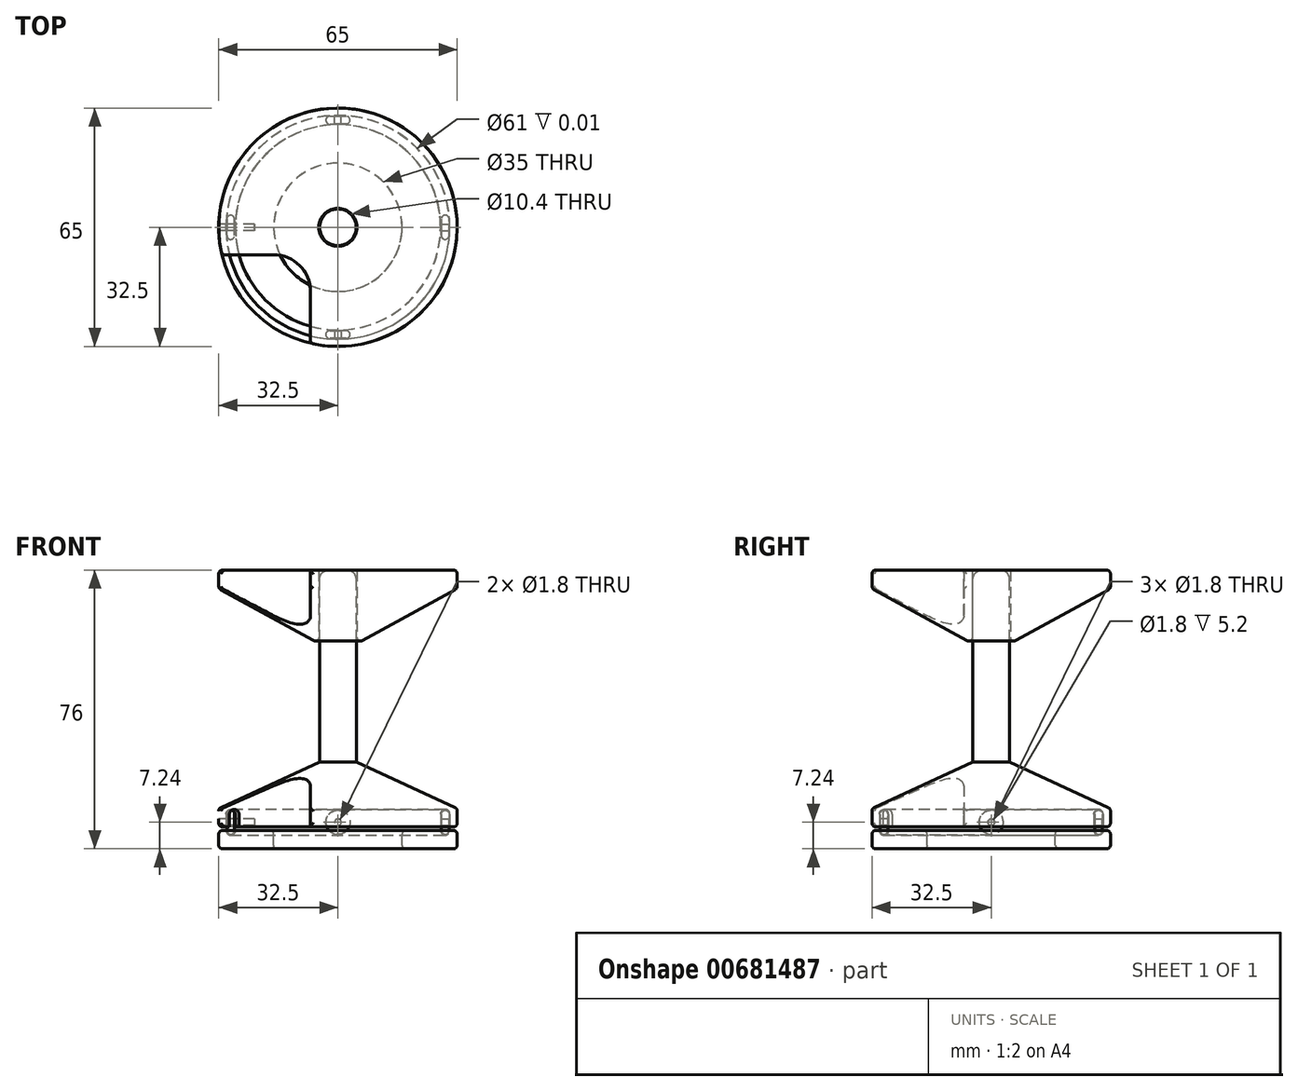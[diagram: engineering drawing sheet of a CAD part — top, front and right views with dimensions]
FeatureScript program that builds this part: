
annotation { "Feature Type Name" : "Feature", "Feature Type Description" : "" }
export const myFeature = defineFeature(function(context is Context, id is Id, definition is map)
    precondition{}
    {
        {
            var Q0;
            Q0=qCreatedBy(makeId("Front.planeOp"),FACE);
            var sketch = newSketch(context, id + "F0", { "sketchPlane" : qUnion([Q0])});
            skLineSegment(sketch, "E0.bottom", {"start": v(0, 2.5) * mm, "end": v(-17.5, 2.5) * mm, "construction": true});
            skLineSegment(sketch, "E0.top", {"start": v(0, -2.5) * mm, "end": v(-17.5, -2.5) * mm, "construction": true});
            skLineSegment(sketch, "E0.left", {"start": v(0, 2.5) * mm, "end": v(0, -2.5) * mm, "construction": true});
            skLineSegment(sketch, "E0.right", {"start": v(-32.5, 2.5) * mm, "end": v(-32.5, -2.5) * mm});
            skPoint(sketch, "E1", {"position": v(-30.5, 2.5) * mm});
            skPoint(sketch, "E2", {"position": v(-28, 2.5) * mm});
            skLineSegment(sketch, "E3", {"start": v(-30.5, 2.5) * mm, "end": v(-30.5, 2.5) * mm});
            skLineSegment(sketch, "E4", {"start": v(-28, 2.5) * mm, "end": v(-28, 2.5) * mm});
            skLineSegment(sketch, "E5", {"start": v(-30.5, 2.5) * mm, "end": v(-28, 2.5) * mm, "construction": true});
            skArc(sketch, "E6", {"start": v(-30.5, 2.5) * mm, "mid": v(-29.25, 1.24) * mm, "end": v(-28, 2.5) * mm});
            skLineSegment(sketch, "E7.trimOffspring", {"start": v(-30.5, 2.5) * mm, "end": v(-32.5, 2.5) * mm});
            skLineSegment(sketch, "E8", {"start": v(-17.5, 2.5) * mm, "end": v(-17.5, -2.5) * mm});
            skLineSegment(sketch, "E9", {"start": v(-17.5, 2.5) * mm, "end": v(-28, 2.5) * mm});
            skLineSegment(sketch, "E10", {"start": v(-17.5, -2.5) * mm, "end": v(-32.5, -2.5) * mm});
            skSolve(sketch);
        }
        {
            var Q0;
            Q0 = qSketchRegion(id + "F0", true);
            var Q1;
            Q1=sQuery(id+"F0.wireOp",EDGE,"E0.left");
            revolve(context, id + "F1", {"entities" : qUnion([Q0]), "axis" : qUnion([Q1]), "revolveType" : RevolveType.FULL});
        }
        {
            var Q0;
            Q0=makeQuery(id+"F1.opRevolve","SWEPT_EDGE",EDGE,{"disambiguationData":[OSD([sQuery(id+"F0.wireOp",EDGE,"E0.right"),sQuery(id+"F0.wireOp",EDGE,"E7.trimOffspring")])]});
            var Q1;
            Q1=makeQuery(id+"F1.opRevolve","SWEPT_EDGE",EDGE,{"disambiguationData":[OSD([sQuery(id+"F0.wireOp",EDGE,"E8"),sQuery(id+"F0.wireOp",EDGE,"E9")])]});
            var Q2;
            Q2=makeQuery(id+"F1.opRevolve","SWEPT_EDGE",EDGE,{"disambiguationData":[OSD([sQuery(id+"F0.wireOp",EDGE,"E0.right"),sQuery(id+"F0.wireOp",EDGE,"E10")])]});
            var Q3;
            Q3=makeQuery(id+"F1.opRevolve","SWEPT_EDGE",EDGE,{"disambiguationData":[OSD([sQuery(id+"F0.wireOp",EDGE,"E8"),sQuery(id+"F0.wireOp",EDGE,"E10")])]});
            fillet(context, id + "F2", {"entities" : qUnion([Q0, Q1, Q2, Q3]), "radius" : 1 * mm, "tangentPropagation" : true, "allowEdgeOverflow" : false});
        }
        {
            var Q0;
            Q0=qCreatedBy(makeId("Front.planeOp"),FACE);
            var sketch = newSketch(context, id + "F3", { "sketchPlane" : qUnion([Q0])});
            skLineSegment(sketch, "E11.bottom", {"start": v(0, 8.5) * mm, "end": v(-32.5, 8.5) * mm, "construction": true});
            skLineSegment(sketch, "E11.top", {"start": v(0, 3.5) * mm, "end": v(-32.5, 3.5) * mm});
            skLineSegment(sketch, "E11.left", {"start": v(0, 23.5) * mm, "end": v(0, 3.5) * mm});
            skLineSegment(sketch, "E11.right", {"start": v(-32.5, 8.5) * mm, "end": v(-32.5, 3.5) * mm});
            skLineSegment(sketch, "E12", {"start": v(-32.5, 8.5) * mm, "end": v(-5, 21.2) * mm});
            skLineSegment(sketch, "E13", {"start": v(0, 23.5) * mm, "end": v(0, 73.5) * mm});
            skLineSegment(sketch, "E14", {"start": v(0, 73.5) * mm, "end": v(-5, 73.5) * mm});
            skLineSegment(sketch, "E15", {"start": v(-5, 73.5) * mm, "end": v(-5, 21.2) * mm});
            skLineSegment(sketch, "E16", {"start": v(-5, 21.2) * mm, "end": v(0, 23.5) * mm, "construction": true});
            skSolve(sketch);
        }
        {
            var Q0;
            Q0 = qSketchRegion(id + "F3", true);
            var Q1;
            Q1=sQuery(id+"F3.wireOp",EDGE,"E11.left");
            revolve(context, id + "F4", {"entities" : qUnion([Q0]), "axis" : qUnion([Q1]), "revolveType" : RevolveType.FULL});
        }
        {
            var Q0;
            Q0=makeQuery(id+"F4.opRevolve","SWEPT_EDGE",EDGE,{"disambiguationData":[OSD([sQuery(id+"F3.wireOp",EDGE,"E14"),sQuery(id+"F3.wireOp",EDGE,"E15")])]});
            fillet(context, id + "F5", {"entities" : qUnion([Q0]), "radius" : 2.5 * mm, "tangentPropagation" : true, "allowEdgeOverflow" : false});
        }
        {
            var Q0;
            Q0=makeQuery(id+"F4.opRevolve","SWEPT_FACE",FACE,{"disambiguationData":[OSD([sQuery(id+"F3.wireOp",EDGE,"E11.top")])]});
            cPlane(context, id + "F6", {"entities" : qUnion([Q0]), "cplaneType" : CPlaneType.OFFSET, "offset" : 0.5 * mm, "width" : 150 * mm, "height" : 150 * mm});
        }
        {
            var Q0;
            Q0=qCreatedBy(id+"F6.planeOp",FACE);
            var sketch = newSketch(context, id + "F7", { "sketchPlane" : qUnion([Q0])});
            skCircle(sketch, "E17", {"center": v(0, 0) * mm, "radius": 32.5 * mm, "construction": true});
            skLineSegment(sketch, "E18", {"start": v(-7.5, 49.07) * mm, "end": v(-7.5, 17.5) * mm});
            skLineSegment(sketch, "E19", {"start": v(-17.5, 7.5) * mm, "end": v(-49.07, 7.5) * mm});
            skLineSegment(sketch, "E20", {"start": v(-49.07, 7.5) * mm, "end": v(-7.5, 49.07) * mm});
            skPoint(sketch, "E21.visualSharp", {"position": v(-7.5, 7.5) * mm});
            skArc(sketch, "E21.filletArc", {"start": v(-17.5, 7.5) * mm, "mid": v(-10.43, 10.43) * mm, "end": v(-7.5, 17.5) * mm});
            skSolve(sketch);
        }
        {
            var Q0;
            Q0 = qSketchRegion(id + "F7", true);
            extrude(context, id + "F8", {"entities" : qUnion([Q0]), "operationType" : NewBodyOperationType.REMOVE, "oppositeDirection" : true, "depth" : 25 * mm, "offsetDistance" : 25 * mm});
        }
        {
            var Q0;
            Q0=makeQuery(id+"F4.opRevolve","SWEPT_EDGE",EDGE,{"disambiguationData":[OSD([sQuery(id+"F3.wireOp",EDGE,"E11.right"),sQuery(id+"F3.wireOp",EDGE,"E12")])]});
            var Q1;
            Q1=makeQuery(id+"F4.opRevolve","SWEPT_EDGE",EDGE,{"disambiguationData":[OSD([sQuery(id+"F3.wireOp",EDGE,"E11.top"),sQuery(id+"F3.wireOp",EDGE,"E11.right")])]});
            var Q2;
            {var subQ0=sQuery(id+"F7.wireOp",EDGE,"E19");Q2=makeQuery(id+"FT7dUQ1MtdXTtgQ_2.2.F8.boolean.opBoolean","INTERSECT",EDGE,{"derivedFrom":[makeQuery(id+"FT7dUQ1MtdXTtgQ_2.1.F8.boolean.opBoolean","SPLIT",FACE,{"disambiguationData":[TD([makeQuery(id+"F8.boolean.opBoolean","COPY",FACE,{"derivedFrom":makeQuery(id+"F8.opExtrude","SWEPT_FACE",FACE,{"disambiguationData":[OSD([subQ0])]})})])],"derivedFrom":makeQuery(id+"F4.opRevolve","SWEPT_FACE",FACE,{"disambiguationData":[OSD([sQuery(id+"F3.wireOp",EDGE,"E11.right")])]})}),makeQuery(id+"FT7dUQ1MtdXTtgQ_2.2.F8.opExtrude","SWEPT_FACE",FACE,{"disambiguationData":[OSD([subQ0])]})]});}
            var Q3;
            Q3=makeQuery(id+"FT7dUQ1MtdXTtgQ_2.1.F8.boolean.opBoolean","INTERSECT",EDGE,{"derivedFrom":[makeQuery(id+"F4.opRevolve","SWEPT_FACE",FACE,{"disambiguationData":[OSD([sQuery(id+"F3.wireOp",EDGE,"E11.right")])]}),makeQuery(id+"FT7dUQ1MtdXTtgQ_2.1.F8.opExtrude","SWEPT_FACE",FACE,{"disambiguationData":[OSD([sQuery(id+"F7.wireOp",EDGE,"E18")])]})]});
            var Q4;
            Q4=makeQuery(id+"FT7dUQ1MtdXTtgQ_2.1.F8.boolean.opBoolean","INTERSECT",EDGE,{"derivedFrom":[makeQuery(id+"F4.opRevolve","SWEPT_FACE",FACE,{"disambiguationData":[OSD([sQuery(id+"F3.wireOp",EDGE,"E12")])]}),makeQuery(id+"FT7dUQ1MtdXTtgQ_2.1.F8.opExtrude","SWEPT_FACE",FACE,{"disambiguationData":[OSD([sQuery(id+"F7.wireOp",EDGE,"E21.filletArc")])]})]});
            var Q5;
            Q5=makeQuery(id+"FT7dUQ1MtdXTtgQ_2.1.F8.boolean.opBoolean","INTERSECT",EDGE,{"derivedFrom":[makeQuery(id+"F4.opRevolve","SWEPT_FACE",FACE,{"disambiguationData":[OSD([sQuery(id+"F3.wireOp",EDGE,"E11.right")])]}),makeQuery(id+"FT7dUQ1MtdXTtgQ_2.1.F8.opExtrude","SWEPT_FACE",FACE,{"disambiguationData":[OSD([sQuery(id+"F7.wireOp",EDGE,"E19")])]})]});
            var Q6;
            Q6=makeQuery(id+"F8.boolean.opBoolean","INTERSECT",EDGE,{"derivedFrom":[makeQuery(id+"F4.opRevolve","SWEPT_FACE",FACE,{"disambiguationData":[OSD([sQuery(id+"F3.wireOp",EDGE,"E11.right")])]}),makeQuery(id+"F8.opExtrude","SWEPT_FACE",FACE,{"disambiguationData":[OSD([sQuery(id+"F7.wireOp",EDGE,"E18")])]})]});
            var Q7;
            Q7=makeQuery(id+"F8.boolean.opBoolean","INTERSECT",EDGE,{"derivedFrom":[makeQuery(id+"F4.opRevolve","SWEPT_FACE",FACE,{"disambiguationData":[OSD([sQuery(id+"F3.wireOp",EDGE,"E12")])]}),makeQuery(id+"F8.opExtrude","SWEPT_FACE",FACE,{"disambiguationData":[OSD([sQuery(id+"F7.wireOp",EDGE,"E21.filletArc")])]})]});
            var Q8;
            Q8=makeQuery(id+"F8.boolean.opBoolean","INTERSECT",EDGE,{"derivedFrom":[makeQuery(id+"F4.opRevolve","SWEPT_FACE",FACE,{"disambiguationData":[OSD([sQuery(id+"F3.wireOp",EDGE,"E11.right")])]}),makeQuery(id+"F8.opExtrude","SWEPT_FACE",FACE,{"disambiguationData":[OSD([sQuery(id+"F7.wireOp",EDGE,"E19")])]})]});
            var Q9;
            {var subQ0=sQuery(id+"F7.wireOp",EDGE,"E18");var subQ3=makeQuery(id+"F8.boolean.opBoolean","COPY",FACE,{"derivedFrom":makeQuery(id+"F8.opExtrude","SWEPT_FACE",FACE,{"disambiguationData":[OSD([sQuery(id+"F7.wireOp",EDGE,"E19")])]})});Q9=makeQuery(id+"FT7dUQ1MtdXTtgQ_2.3.F8.boolean.opBoolean","INTERSECT",EDGE,{"derivedFrom":[makeQuery(id+"FT7dUQ1MtdXTtgQ_2.2.F8.boolean.opBoolean","SPLIT",FACE,{"disambiguationData":[TD([subQ3])],"derivedFrom":makeQuery(id+"FT7dUQ1MtdXTtgQ_2.1.F8.boolean.opBoolean","SPLIT",FACE,{"disambiguationData":[TD([subQ3])],"derivedFrom":makeQuery(id+"F4.opRevolve","SWEPT_FACE",FACE,{"disambiguationData":[OSD([sQuery(id+"F3.wireOp",EDGE,"E11.right")])]})})}),makeQuery(id+"FT7dUQ1MtdXTtgQ_2.3.F8.opExtrude","SWEPT_FACE",FACE,{"disambiguationData":[OSD([subQ0])]})]});}
            var Q10;
            Q10=makeQuery(id+"FT7dUQ1MtdXTtgQ_2.3.F8.boolean.opBoolean","INTERSECT",EDGE,{"derivedFrom":[makeQuery(id+"F4.opRevolve","SWEPT_FACE",FACE,{"disambiguationData":[OSD([sQuery(id+"F3.wireOp",EDGE,"E12")])]}),makeQuery(id+"FT7dUQ1MtdXTtgQ_2.3.F8.opExtrude","SWEPT_FACE",FACE,{"disambiguationData":[OSD([sQuery(id+"F7.wireOp",EDGE,"E21.filletArc")])]})]});
            var Q11;
            {var subQ0=sQuery(id+"F7.wireOp",EDGE,"E19");var subQ3=makeQuery(id+"F8.boolean.opBoolean","COPY",FACE,{"derivedFrom":makeQuery(id+"F8.opExtrude","SWEPT_FACE",FACE,{"disambiguationData":[OSD([subQ0])]})});Q11=makeQuery(id+"FT7dUQ1MtdXTtgQ_2.3.F8.boolean.opBoolean","INTERSECT",EDGE,{"derivedFrom":[makeQuery(id+"FT7dUQ1MtdXTtgQ_2.2.F8.boolean.opBoolean","SPLIT",FACE,{"disambiguationData":[TD([subQ3])],"derivedFrom":makeQuery(id+"FT7dUQ1MtdXTtgQ_2.1.F8.boolean.opBoolean","SPLIT",FACE,{"disambiguationData":[TD([subQ3])],"derivedFrom":makeQuery(id+"F4.opRevolve","SWEPT_FACE",FACE,{"disambiguationData":[OSD([sQuery(id+"F3.wireOp",EDGE,"E11.right")])]})})}),makeQuery(id+"FT7dUQ1MtdXTtgQ_2.3.F8.opExtrude","SWEPT_FACE",FACE,{"disambiguationData":[OSD([subQ0])]})]});}
            var Q12;
            {var subQ0=sQuery(id+"F7.wireOp",EDGE,"E18");Q12=makeQuery(id+"FT7dUQ1MtdXTtgQ_2.2.F8.boolean.opBoolean","INTERSECT",EDGE,{"derivedFrom":[makeQuery(id+"FT7dUQ1MtdXTtgQ_2.1.F8.boolean.opBoolean","SPLIT",FACE,{"disambiguationData":[TD([makeQuery(id+"F8.boolean.opBoolean","COPY",FACE,{"derivedFrom":makeQuery(id+"F8.opExtrude","SWEPT_FACE",FACE,{"disambiguationData":[OSD([sQuery(id+"F7.wireOp",EDGE,"E19")])]})})])],"derivedFrom":makeQuery(id+"F4.opRevolve","SWEPT_FACE",FACE,{"disambiguationData":[OSD([sQuery(id+"F3.wireOp",EDGE,"E11.right")])]})}),makeQuery(id+"FT7dUQ1MtdXTtgQ_2.2.F8.opExtrude","SWEPT_FACE",FACE,{"disambiguationData":[OSD([subQ0])]})]});}
            var Q13;
            Q13=makeQuery(id+"FT7dUQ1MtdXTtgQ_2.2.F8.boolean.opBoolean","INTERSECT",EDGE,{"derivedFrom":[makeQuery(id+"F4.opRevolve","SWEPT_FACE",FACE,{"disambiguationData":[OSD([sQuery(id+"F3.wireOp",EDGE,"E12")])]}),makeQuery(id+"FT7dUQ1MtdXTtgQ_2.2.F8.opExtrude","SWEPT_FACE",FACE,{"disambiguationData":[OSD([sQuery(id+"F7.wireOp",EDGE,"E21.filletArc")])]})]});
            var Q14;
            Q14=makeQuery(id+"FT7dUQ1MtdXTtgQ_2.2.F8.boolean.opBoolean","INTERSECT",EDGE,{"derivedFrom":[makeQuery(id+"F4.opRevolve","SWEPT_FACE",FACE,{"disambiguationData":[OSD([sQuery(id+"F3.wireOp",EDGE,"E11.top")])]}),makeQuery(id+"FT7dUQ1MtdXTtgQ_2.2.F8.opExtrude","SWEPT_FACE",FACE,{"disambiguationData":[OSD([sQuery(id+"F7.wireOp",EDGE,"E21.filletArc")])]})]});
            var Q15;
            Q15=makeQuery(id+"FT7dUQ1MtdXTtgQ_2.3.F8.boolean.opBoolean","INTERSECT",EDGE,{"derivedFrom":[makeQuery(id+"F4.opRevolve","SWEPT_FACE",FACE,{"disambiguationData":[OSD([sQuery(id+"F3.wireOp",EDGE,"E11.top")])]}),makeQuery(id+"FT7dUQ1MtdXTtgQ_2.3.F8.opExtrude","SWEPT_FACE",FACE,{"disambiguationData":[OSD([sQuery(id+"F7.wireOp",EDGE,"E21.filletArc")])]})]});
            var Q16;
            Q16=makeQuery(id+"F8.boolean.opBoolean","INTERSECT",EDGE,{"derivedFrom":[makeQuery(id+"F4.opRevolve","SWEPT_FACE",FACE,{"disambiguationData":[OSD([sQuery(id+"F3.wireOp",EDGE,"E11.top")])]}),makeQuery(id+"F8.opExtrude","SWEPT_FACE",FACE,{"disambiguationData":[OSD([sQuery(id+"F7.wireOp",EDGE,"E21.filletArc")])]})]});
            var Q17;
            Q17=makeQuery(id+"FT7dUQ1MtdXTtgQ_2.1.F8.boolean.opBoolean","INTERSECT",EDGE,{"derivedFrom":[makeQuery(id+"F4.opRevolve","SWEPT_FACE",FACE,{"disambiguationData":[OSD([sQuery(id+"F3.wireOp",EDGE,"E11.top")])]}),makeQuery(id+"FT7dUQ1MtdXTtgQ_2.1.F8.opExtrude","SWEPT_FACE",FACE,{"disambiguationData":[OSD([sQuery(id+"F7.wireOp",EDGE,"E21.filletArc")])]})]});
            fillet(context, id + "F9", {"entities" : qUnion([Q0, Q1, Q2, Q3, Q4, Q5, Q6, Q7, Q8, Q9, Q10, Q11, Q12, Q13, Q14, Q15, Q16, Q17]), "radius" : 1 * mm, "tangentPropagation" : true, "allowEdgeOverflow" : false});
        }
        {
            var Q0;
            Q0=qCreatedBy(makeId("Front.planeOp"),FACE);
            var sketch = newSketch(context, id + "F10", { "sketchPlane" : qUnion([Q0])});
            skLineSegment(sketch, "E22.bottom", {"start": v(-28, 7) * mm, "end": v(-30.5, 7) * mm, "construction": true});
            skLineSegment(sketch, "E22.top", {"start": v(-28, 2.5) * mm, "end": v(-30.5, 2.5) * mm, "construction": true});
            skLineSegment(sketch, "E22.left", {"start": v(-28, 7) * mm, "end": v(-28, 2.5) * mm});
            skLineSegment(sketch, "E22.right", {"start": v(-30.5, 7) * mm, "end": v(-30.5, 2.5) * mm});
            skArc(sketch, "E23", {"start": v(-30.5, 2.5) * mm, "mid": v(-29.25, 1.24) * mm, "end": v(-28, 2.5) * mm});
            skArc(sketch, "E24", {"start": v(-28, 7) * mm, "mid": v(-29.25, 8.24) * mm, "end": v(-30.5, 7) * mm});
            skLineSegment(sketch, "E25", {"start": v(-30.5, 4.74) * mm, "end": v(-28, 4.74) * mm, "construction": true});
            skLineSegment(sketch, "E26.bottom", {"start": v(-30.5, 5.64) * mm, "end": v(-28, 5.64) * mm, "construction": true});
            skLineSegment(sketch, "E26.top", {"start": v(-30.5, 3.84) * mm, "end": v(-28, 3.84) * mm, "construction": true});
            skLineSegment(sketch, "E26.left", {"start": v(-30.5, 5.64) * mm, "end": v(-30.5, 3.84) * mm, "construction": true});
            skLineSegment(sketch, "E26.right", {"start": v(-28, 5.64) * mm, "end": v(-28, 3.84) * mm, "construction": true});
            skSolve(sketch);
        }
        {
            var Q0;
            Q0 = qSketchRegion(id + "F10", true);
            var Q1;
            Q1=sQuery(id+"F3.wireOp",EDGE,"E11.left");
            revolve(context, id + "F11", {"operationType" : NewBodyOperationType.REMOVE, "entities" : qUnion([Q0]), "axis" : qUnion([Q1]), "revolveType" : RevolveType.FULL, "oppositeDirection" : true});
        }
        {
            var Q0;
            Q0=qCreatedBy(makeId("Front.planeOp"),FACE);
            var sketch = newSketch(context, id + "F12", { "sketchPlane" : qUnion([Q0])});
            skLineSegment(sketch, "E27.bottom", {"start": v(-30.3, 5.64) * mm, "end": v(-28.2, 5.64) * mm});
            skLineSegment(sketch, "E27.top", {"start": v(-30.3, 7) * mm, "end": v(-28.2, 7) * mm, "construction": true});
            skLineSegment(sketch, "E27.left", {"start": v(-30.3, 5.64) * mm, "end": v(-30.3, 7) * mm});
            skLineSegment(sketch, "E27.right", {"start": v(-28.2, 5.64) * mm, "end": v(-28.2, 7) * mm});
            skArc(sketch, "E28", {"start": v(-28.2, 7) * mm, "mid": v(-29.25, 8.04) * mm, "end": v(-30.3, 7) * mm});
            skSolve(sketch);
        }
        {
            var Q0;
            Q0 = qSketchRegion(id + "F12", true);
            var Q1;
            Q1=sQuery(id+"F10.wireOp",EDGE,"E25");
            revolve(context, id + "F13", {"entities" : qUnion([Q0]), "axis" : qUnion([Q1]), "revolveType" : RevolveType.FULL});
        }
        {
            var Q0;
            Q0=makeQuery(id+"F13.opRevolve","SWEPT_BODY",BODY,{"disambiguationData":[OSD([sQuery(id+"F12.wireOp",EDGE,"E27.bottom"),sQuery(id+"F12.wireOp",EDGE,"E27.left"),sQuery(id+"F12.wireOp",EDGE,"E27.right"),sQuery(id+"F12.wireOp",EDGE,"E28")])]});
            var Q1;
            Q1=sQuery(id+"F3.wireOp",EDGE,"E13");
            circularPattern(context, id + "F14", {"entities" : qUnion([Q0]), "axis" : qUnion([Q1]), "angle" : 360 * degree, "instanceCount" : 4, "equalSpace" : true});
        }
        {
            var Q0;
            Q0=makeQuery(id+"F13.opRevolve","SWEPT_FACE",FACE,{"disambiguationData":[OSD([sQuery(id+"F12.wireOp",EDGE,"E27.left")])]});
            var sketch = newSketch(context, id + "F15", { "sketchPlane" : qUnion([Q0])});
            skCircle(sketch, "E29", {"center": v(0, 4.74) * mm, "radius": 0.9 * mm});
            skSolve(sketch);
        }
        {
            var Q0;
            Q0 = qSketchRegion(id + "F15", true);
            extrude(context, id + "F16", {"entities" : qUnion([Q0]), "operationType" : NewBodyOperationType.REMOVE, "endBound" : BoundingType.SYMMETRIC, "oppositeDirection" : true, "depth" : 15 * mm, "offsetDistance" : 25 * mm});
        }
        {
            var Q0;
            Q0=qCreatedBy(makeId("Front.planeOp"),FACE);
            var sketch = newSketch(context, id + "F17", { "sketchPlane" : qUnion([Q0])});
            skLineSegment(sketch, "E30.bottom", {"start": v(-5.2, 73.5) * mm, "end": v(-32.5, 73.5) * mm});
            skLineSegment(sketch, "E30.top", {"start": v(-5.2, 68.5) * mm, "end": v(-32.5, 68.5) * mm, "construction": true});
            skLineSegment(sketch, "E30.left", {"start": v(-5.2, 73.5) * mm, "end": v(-5.2, 68.5) * mm});
            skLineSegment(sketch, "E30.right", {"start": v(-32.5, 73.5) * mm, "end": v(-32.5, 68.5) * mm});
            skLineSegment(sketch, "E31", {"start": v(-5.2, 68.5) * mm, "end": v(-5.2, 53.5) * mm});
            skLineSegment(sketch, "E32", {"start": v(-5.2, 53.5) * mm, "end": v(-32.5, 68.5) * mm});
            skSolve(sketch);
        }
        {
            var Q0;
            Q0 = qSketchRegion(id + "F17", true);
            var Q1;
            Q1=sQuery(id+"F3.wireOp",EDGE,"E13");
            revolve(context, id + "F18", {"entities" : qUnion([Q0]), "axis" : qUnion([Q1]), "revolveType" : RevolveType.FULL});
        }
        {
            var Q0;
            Q0 = qSketchRegion(id + "F7", true);
            extrude(context, id + "F19", {"entities" : qUnion([Q0]), "operationType" : NewBodyOperationType.REMOVE, "endBound" : BoundingType.THROUGH_ALL, "oppositeDirection" : true, "depth" : 25 * mm, "offsetDistance" : 25 * mm});
        }
        {
            var Q0;
            Q0=makeQuery(id+"F18.opRevolve","SWEPT_EDGE",EDGE,{"disambiguationData":[OSD([sQuery(id+"F17.wireOp",EDGE,"E31"),sQuery(id+"F17.wireOp",EDGE,"E32")])]});
            var Q1;
            Q1=makeQuery(id+"F19.boolean.opBoolean","INTERSECT",EDGE,{"derivedFrom":[makeQuery(id+"F18.opRevolve","SWEPT_FACE",FACE,{"disambiguationData":[OSD([sQuery(id+"F17.wireOp",EDGE,"E32")])]}),makeQuery(id+"F19.opExtrude","SWEPT_FACE",FACE,{"disambiguationData":[OSD([sQuery(id+"F7.wireOp",EDGE,"E21.filletArc")])]})]});
            var Q2;
            Q2=makeQuery(id+"FgBuMioiOsYxcSs_4.1.F19.boolean.opBoolean","INTERSECT",EDGE,{"derivedFrom":[makeQuery(id+"F18.opRevolve","SWEPT_FACE",FACE,{"disambiguationData":[OSD([sQuery(id+"F17.wireOp",EDGE,"E32")])]}),makeQuery(id+"FgBuMioiOsYxcSs_4.1.F19.opExtrude","SWEPT_FACE",FACE,{"disambiguationData":[OSD([sQuery(id+"F7.wireOp",EDGE,"E21.filletArc")])]})]});
            var Q3;
            Q3=makeQuery(id+"FgBuMioiOsYxcSs_4.3.F19.boolean.opBoolean","INTERSECT",EDGE,{"derivedFrom":[makeQuery(id+"F18.opRevolve","SWEPT_FACE",FACE,{"disambiguationData":[OSD([sQuery(id+"F17.wireOp",EDGE,"E32")])]}),makeQuery(id+"FgBuMioiOsYxcSs_4.3.F19.opExtrude","SWEPT_FACE",FACE,{"disambiguationData":[OSD([sQuery(id+"F7.wireOp",EDGE,"E21.filletArc")])]})]});
            var Q4;
            Q4=makeQuery(id+"FgBuMioiOsYxcSs_4.2.F19.boolean.opBoolean","INTERSECT",EDGE,{"derivedFrom":[makeQuery(id+"F18.opRevolve","SWEPT_FACE",FACE,{"disambiguationData":[OSD([sQuery(id+"F17.wireOp",EDGE,"E32")])]}),makeQuery(id+"FgBuMioiOsYxcSs_4.2.F19.opExtrude","SWEPT_FACE",FACE,{"disambiguationData":[OSD([sQuery(id+"F7.wireOp",EDGE,"E21.filletArc")])]})]});
            var Q5;
            Q5=makeQuery(id+"FgBuMioiOsYxcSs_4.1.F19.boolean.opBoolean","INTERSECT",EDGE,{"derivedFrom":[makeQuery(id+"F18.opRevolve","SWEPT_FACE",FACE,{"disambiguationData":[OSD([sQuery(id+"F17.wireOp",EDGE,"E30.bottom")])]}),makeQuery(id+"FgBuMioiOsYxcSs_4.1.F19.opExtrude","SWEPT_FACE",FACE,{"disambiguationData":[OSD([sQuery(id+"F7.wireOp",EDGE,"E21.filletArc")])]})]});
            var Q6;
            Q6=makeQuery(id+"F19.boolean.opBoolean","INTERSECT",EDGE,{"derivedFrom":[makeQuery(id+"F18.opRevolve","SWEPT_FACE",FACE,{"disambiguationData":[OSD([sQuery(id+"F17.wireOp",EDGE,"E30.bottom")])]}),makeQuery(id+"F19.opExtrude","SWEPT_FACE",FACE,{"disambiguationData":[OSD([sQuery(id+"F7.wireOp",EDGE,"E21.filletArc")])]})]});
            var Q7;
            Q7=makeQuery(id+"FgBuMioiOsYxcSs_4.3.F19.boolean.opBoolean","INTERSECT",EDGE,{"derivedFrom":[makeQuery(id+"F18.opRevolve","SWEPT_FACE",FACE,{"disambiguationData":[OSD([sQuery(id+"F17.wireOp",EDGE,"E30.bottom")])]}),makeQuery(id+"FgBuMioiOsYxcSs_4.3.F19.opExtrude","SWEPT_FACE",FACE,{"disambiguationData":[OSD([sQuery(id+"F7.wireOp",EDGE,"E21.filletArc")])]})]});
            var Q8;
            Q8=makeQuery(id+"FgBuMioiOsYxcSs_4.2.F19.boolean.opBoolean","INTERSECT",EDGE,{"derivedFrom":[makeQuery(id+"F18.opRevolve","SWEPT_FACE",FACE,{"disambiguationData":[OSD([sQuery(id+"F17.wireOp",EDGE,"E30.bottom")])]}),makeQuery(id+"FgBuMioiOsYxcSs_4.2.F19.opExtrude","SWEPT_FACE",FACE,{"disambiguationData":[OSD([sQuery(id+"F7.wireOp",EDGE,"E21.filletArc")])]})]});
            var Q9;
            {var subQ0=sQuery(id+"F17.wireOp",EDGE,"E30.bottom");var subQ2=sQuery(id+"F17.wireOp",EDGE,"E30.right");var subQ4=makeQuery(id+"FgBuMioiOsYxcSs_4.1.F19.opExtrude","SWEPT_FACE",FACE,{"disambiguationData":[OSD([sQuery(id+"F7.wireOp",EDGE,"E18")])]});var subQ5=sQuery(id+"F7.wireOp",EDGE,"E19");Q9=makeQuery(id+"FgBuMioiOsYxcSs_4.2.F19.boolean.opBoolean","SPLIT",EDGE,{"disambiguationData":[TD([makeQuery(id+"FgBuMioiOsYxcSs_4.1.F19.boolean.opBoolean","COPY",FACE,{"derivedFrom":subQ4})])],"derivedFrom":makeQuery(id+"FgBuMioiOsYxcSs_4.1.F19.boolean.opBoolean","SPLIT",EDGE,{"disambiguationData":[TD([makeQuery(id+"F19.boolean.opBoolean","COPY",FACE,{"derivedFrom":makeQuery(id+"F19.opExtrude","SWEPT_FACE",FACE,{"disambiguationData":[OSD([subQ5])]})})])],"derivedFrom":makeQuery(id+"F18.opRevolve","SWEPT_EDGE",EDGE,{"disambiguationData":[OSD([subQ0,subQ2])]})})});}
            var Q10;
            {var subQ0=sQuery(id+"F17.wireOp",EDGE,"E30.bottom");var subQ1=sQuery(id+"F17.wireOp",EDGE,"E30.right");Q10=makeQuery(id+"FgBuMioiOsYxcSs_4.1.F19.boolean.opBoolean","SPLIT",EDGE,{"disambiguationData":[TD([makeQuery(id+"F19.boolean.opBoolean","COPY",FACE,{"derivedFrom":makeQuery(id+"F19.opExtrude","SWEPT_FACE",FACE,{"disambiguationData":[OSD([sQuery(id+"F7.wireOp",EDGE,"E18")])]})})])],"derivedFrom":makeQuery(id+"F18.opRevolve","SWEPT_EDGE",EDGE,{"disambiguationData":[OSD([subQ0,subQ1])]})});}
            var Q11;
            {var subQ0=sQuery(id+"F17.wireOp",EDGE,"E30.bottom");var subQ2=sQuery(id+"F17.wireOp",EDGE,"E30.right");var subQ5=makeQuery(id+"F19.boolean.opBoolean","COPY",FACE,{"derivedFrom":makeQuery(id+"F19.opExtrude","SWEPT_FACE",FACE,{"disambiguationData":[OSD([sQuery(id+"F7.wireOp",EDGE,"E19")])]})});Q11=makeQuery(id+"FgBuMioiOsYxcSs_4.3.F19.boolean.opBoolean","SPLIT",EDGE,{"disambiguationData":[TD([subQ5])],"derivedFrom":makeQuery(id+"FgBuMioiOsYxcSs_4.2.F19.boolean.opBoolean","SPLIT",EDGE,{"disambiguationData":[TD([subQ5])],"derivedFrom":makeQuery(id+"FgBuMioiOsYxcSs_4.1.F19.boolean.opBoolean","SPLIT",EDGE,{"disambiguationData":[TD([subQ5])],"derivedFrom":makeQuery(id+"F18.opRevolve","SWEPT_EDGE",EDGE,{"disambiguationData":[OSD([subQ0,subQ2])]})})})});}
            var Q12;
            {var subQ0=sQuery(id+"F17.wireOp",EDGE,"E30.bottom");var subQ2=sQuery(id+"F7.wireOp",EDGE,"E19");var subQ3=sQuery(id+"F17.wireOp",EDGE,"E30.right");var subQ5=sQuery(id+"F7.wireOp",EDGE,"E18");var subQ6=makeQuery(id+"FgBuMioiOsYxcSs_4.2.F19.opExtrude","SWEPT_FACE",FACE,{"disambiguationData":[OSD([subQ5])]});var subQ7=makeQuery(id+"F19.boolean.opBoolean","COPY",FACE,{"derivedFrom":makeQuery(id+"F19.opExtrude","SWEPT_FACE",FACE,{"disambiguationData":[OSD([subQ2])]})});Q12=makeQuery(id+"FgBuMioiOsYxcSs_4.3.F19.boolean.opBoolean","SPLIT",EDGE,{"disambiguationData":[TD([makeQuery(id+"FgBuMioiOsYxcSs_4.2.F19.boolean.opBoolean","COPY",FACE,{"derivedFrom":subQ6})])],"derivedFrom":makeQuery(id+"FgBuMioiOsYxcSs_4.2.F19.boolean.opBoolean","SPLIT",EDGE,{"disambiguationData":[TD([subQ7])],"derivedFrom":makeQuery(id+"FgBuMioiOsYxcSs_4.1.F19.boolean.opBoolean","SPLIT",EDGE,{"disambiguationData":[TD([subQ7])],"derivedFrom":makeQuery(id+"F18.opRevolve","SWEPT_EDGE",EDGE,{"disambiguationData":[OSD([subQ0,subQ3])]})})})});}
            var Q13;
            {var subQ0=sQuery(id+"F7.wireOp",EDGE,"E19");Q13=makeQuery(id+"FgBuMioiOsYxcSs_4.2.F19.boolean.opBoolean","INTERSECT",EDGE,{"derivedFrom":[makeQuery(id+"FgBuMioiOsYxcSs_4.1.F19.boolean.opBoolean","SPLIT",FACE,{"disambiguationData":[TD([makeQuery(id+"F19.boolean.opBoolean","COPY",FACE,{"derivedFrom":makeQuery(id+"F19.opExtrude","SWEPT_FACE",FACE,{"disambiguationData":[OSD([subQ0])]})})])],"derivedFrom":makeQuery(id+"F18.opRevolve","SWEPT_FACE",FACE,{"disambiguationData":[OSD([sQuery(id+"F17.wireOp",EDGE,"E30.right")])]})}),makeQuery(id+"FgBuMioiOsYxcSs_4.2.F19.opExtrude","SWEPT_FACE",FACE,{"disambiguationData":[OSD([subQ0])]})]});}
            var Q14;
            {var subQ0=sQuery(id+"F7.wireOp",EDGE,"E18");Q14=makeQuery(id+"FgBuMioiOsYxcSs_4.2.F19.boolean.opBoolean","INTERSECT",EDGE,{"derivedFrom":[makeQuery(id+"FgBuMioiOsYxcSs_4.1.F19.boolean.opBoolean","SPLIT",FACE,{"disambiguationData":[TD([makeQuery(id+"F19.boolean.opBoolean","COPY",FACE,{"derivedFrom":makeQuery(id+"F19.opExtrude","SWEPT_FACE",FACE,{"disambiguationData":[OSD([sQuery(id+"F7.wireOp",EDGE,"E19")])]})})])],"derivedFrom":makeQuery(id+"F18.opRevolve","SWEPT_FACE",FACE,{"disambiguationData":[OSD([sQuery(id+"F17.wireOp",EDGE,"E30.right")])]})}),makeQuery(id+"FgBuMioiOsYxcSs_4.2.F19.opExtrude","SWEPT_FACE",FACE,{"disambiguationData":[OSD([subQ0])]})]});}
            var Q15;
            {var subQ0=sQuery(id+"F17.wireOp",EDGE,"E30.right");var subQ2=sQuery(id+"F17.wireOp",EDGE,"E32");var subQ4=sQuery(id+"F7.wireOp",EDGE,"E19");var subQ5=makeQuery(id+"FgBuMioiOsYxcSs_4.1.F19.opExtrude","SWEPT_FACE",FACE,{"disambiguationData":[OSD([sQuery(id+"F7.wireOp",EDGE,"E18")])]});Q15=makeQuery(id+"FgBuMioiOsYxcSs_4.2.F19.boolean.opBoolean","SPLIT",EDGE,{"disambiguationData":[TD([makeQuery(id+"FgBuMioiOsYxcSs_4.1.F19.boolean.opBoolean","COPY",FACE,{"derivedFrom":subQ5})])],"derivedFrom":makeQuery(id+"FgBuMioiOsYxcSs_4.1.F19.boolean.opBoolean","SPLIT",EDGE,{"disambiguationData":[TD([makeQuery(id+"F19.boolean.opBoolean","COPY",FACE,{"derivedFrom":makeQuery(id+"F19.opExtrude","SWEPT_FACE",FACE,{"disambiguationData":[OSD([subQ4])]})})])],"derivedFrom":makeQuery(id+"F18.opRevolve","SWEPT_EDGE",EDGE,{"disambiguationData":[OSD([subQ0,subQ2])]})})});}
            var Q16;
            {var subQ0=sQuery(id+"F17.wireOp",EDGE,"E30.right");var subQ2=sQuery(id+"F17.wireOp",EDGE,"E32");var subQ4=sQuery(id+"F7.wireOp",EDGE,"E18");var subQ5=makeQuery(id+"FgBuMioiOsYxcSs_4.2.F19.opExtrude","SWEPT_FACE",FACE,{"disambiguationData":[OSD([subQ4])]});var subQ6=sQuery(id+"F7.wireOp",EDGE,"E19");var subQ7=makeQuery(id+"F19.boolean.opBoolean","COPY",FACE,{"derivedFrom":makeQuery(id+"F19.opExtrude","SWEPT_FACE",FACE,{"disambiguationData":[OSD([subQ6])]})});Q16=makeQuery(id+"FgBuMioiOsYxcSs_4.3.F19.boolean.opBoolean","SPLIT",EDGE,{"disambiguationData":[TD([makeQuery(id+"FgBuMioiOsYxcSs_4.2.F19.boolean.opBoolean","COPY",FACE,{"derivedFrom":subQ5})])],"derivedFrom":makeQuery(id+"FgBuMioiOsYxcSs_4.2.F19.boolean.opBoolean","SPLIT",EDGE,{"disambiguationData":[TD([subQ7])],"derivedFrom":makeQuery(id+"FgBuMioiOsYxcSs_4.1.F19.boolean.opBoolean","SPLIT",EDGE,{"disambiguationData":[TD([subQ7])],"derivedFrom":makeQuery(id+"F18.opRevolve","SWEPT_EDGE",EDGE,{"disambiguationData":[OSD([subQ0,subQ2])]})})})});}
            var Q17;
            {var subQ0=sQuery(id+"F7.wireOp",EDGE,"E19");var subQ4=makeQuery(id+"F19.boolean.opBoolean","COPY",FACE,{"derivedFrom":makeQuery(id+"F19.opExtrude","SWEPT_FACE",FACE,{"disambiguationData":[OSD([subQ0])]})});Q17=makeQuery(id+"FgBuMioiOsYxcSs_4.3.F19.boolean.opBoolean","INTERSECT",EDGE,{"derivedFrom":[makeQuery(id+"FgBuMioiOsYxcSs_4.2.F19.boolean.opBoolean","SPLIT",FACE,{"disambiguationData":[TD([subQ4])],"derivedFrom":makeQuery(id+"FgBuMioiOsYxcSs_4.1.F19.boolean.opBoolean","SPLIT",FACE,{"disambiguationData":[TD([subQ4])],"derivedFrom":makeQuery(id+"F18.opRevolve","SWEPT_FACE",FACE,{"disambiguationData":[OSD([sQuery(id+"F17.wireOp",EDGE,"E30.right")])]})})}),makeQuery(id+"FgBuMioiOsYxcSs_4.3.F19.opExtrude","SWEPT_FACE",FACE,{"disambiguationData":[OSD([subQ0])]})]});}
            var Q18;
            {var subQ0=sQuery(id+"F7.wireOp",EDGE,"E18");var subQ3=makeQuery(id+"F19.boolean.opBoolean","COPY",FACE,{"derivedFrom":makeQuery(id+"F19.opExtrude","SWEPT_FACE",FACE,{"disambiguationData":[OSD([sQuery(id+"F7.wireOp",EDGE,"E19")])]})});Q18=makeQuery(id+"FgBuMioiOsYxcSs_4.3.F19.boolean.opBoolean","INTERSECT",EDGE,{"derivedFrom":[makeQuery(id+"FgBuMioiOsYxcSs_4.2.F19.boolean.opBoolean","SPLIT",FACE,{"disambiguationData":[TD([subQ3])],"derivedFrom":makeQuery(id+"FgBuMioiOsYxcSs_4.1.F19.boolean.opBoolean","SPLIT",FACE,{"disambiguationData":[TD([subQ3])],"derivedFrom":makeQuery(id+"F18.opRevolve","SWEPT_FACE",FACE,{"disambiguationData":[OSD([sQuery(id+"F17.wireOp",EDGE,"E30.right")])]})})}),makeQuery(id+"FgBuMioiOsYxcSs_4.3.F19.opExtrude","SWEPT_FACE",FACE,{"disambiguationData":[OSD([subQ0])]})]});}
            var Q19;
            {var subQ0=sQuery(id+"F17.wireOp",EDGE,"E30.right");var subQ3=sQuery(id+"F17.wireOp",EDGE,"E32");var subQ5=makeQuery(id+"F19.boolean.opBoolean","COPY",FACE,{"derivedFrom":makeQuery(id+"F19.opExtrude","SWEPT_FACE",FACE,{"disambiguationData":[OSD([sQuery(id+"F7.wireOp",EDGE,"E19")])]})});Q19=makeQuery(id+"FgBuMioiOsYxcSs_4.3.F19.boolean.opBoolean","SPLIT",EDGE,{"disambiguationData":[TD([subQ5])],"derivedFrom":makeQuery(id+"FgBuMioiOsYxcSs_4.2.F19.boolean.opBoolean","SPLIT",EDGE,{"disambiguationData":[TD([subQ5])],"derivedFrom":makeQuery(id+"FgBuMioiOsYxcSs_4.1.F19.boolean.opBoolean","SPLIT",EDGE,{"disambiguationData":[TD([subQ5])],"derivedFrom":makeQuery(id+"F18.opRevolve","SWEPT_EDGE",EDGE,{"disambiguationData":[OSD([subQ0,subQ3])]})})})});}
            var Q20;
            Q20=makeQuery(id+"F19.boolean.opBoolean","INTERSECT",EDGE,{"derivedFrom":[makeQuery(id+"F18.opRevolve","SWEPT_FACE",FACE,{"disambiguationData":[OSD([sQuery(id+"F17.wireOp",EDGE,"E30.right")])]}),makeQuery(id+"F19.opExtrude","SWEPT_FACE",FACE,{"disambiguationData":[OSD([sQuery(id+"F7.wireOp",EDGE,"E19")])]})]});
            var Q21;
            Q21=makeQuery(id+"F19.boolean.opBoolean","INTERSECT",EDGE,{"derivedFrom":[makeQuery(id+"F18.opRevolve","SWEPT_FACE",FACE,{"disambiguationData":[OSD([sQuery(id+"F17.wireOp",EDGE,"E30.right")])]}),makeQuery(id+"F19.opExtrude","SWEPT_FACE",FACE,{"disambiguationData":[OSD([sQuery(id+"F7.wireOp",EDGE,"E18")])]})]});
            var Q22;
            {var subQ0=sQuery(id+"F17.wireOp",EDGE,"E30.right");var subQ1=sQuery(id+"F17.wireOp",EDGE,"E32");Q22=makeQuery(id+"FgBuMioiOsYxcSs_4.1.F19.boolean.opBoolean","SPLIT",EDGE,{"disambiguationData":[TD([makeQuery(id+"F19.boolean.opBoolean","COPY",FACE,{"derivedFrom":makeQuery(id+"F19.opExtrude","SWEPT_FACE",FACE,{"disambiguationData":[OSD([sQuery(id+"F7.wireOp",EDGE,"E18")])]})})])],"derivedFrom":makeQuery(id+"F18.opRevolve","SWEPT_EDGE",EDGE,{"disambiguationData":[OSD([subQ0,subQ1])]})});}
            var Q23;
            Q23=makeQuery(id+"FgBuMioiOsYxcSs_4.1.F19.boolean.opBoolean","INTERSECT",EDGE,{"derivedFrom":[makeQuery(id+"F18.opRevolve","SWEPT_FACE",FACE,{"disambiguationData":[OSD([sQuery(id+"F17.wireOp",EDGE,"E30.right")])]}),makeQuery(id+"FgBuMioiOsYxcSs_4.1.F19.opExtrude","SWEPT_FACE",FACE,{"disambiguationData":[OSD([sQuery(id+"F7.wireOp",EDGE,"E19")])]})]});
            var Q24;
            Q24=makeQuery(id+"FgBuMioiOsYxcSs_4.1.F19.boolean.opBoolean","INTERSECT",EDGE,{"derivedFrom":[makeQuery(id+"F18.opRevolve","SWEPT_FACE",FACE,{"disambiguationData":[OSD([sQuery(id+"F17.wireOp",EDGE,"E30.right")])]}),makeQuery(id+"FgBuMioiOsYxcSs_4.1.F19.opExtrude","SWEPT_FACE",FACE,{"disambiguationData":[OSD([sQuery(id+"F7.wireOp",EDGE,"E18")])]})]});
            fillet(context, id + "F20", {"entities" : qUnion([Q0, Q1, Q2, Q3, Q4, Q5, Q6, Q7, Q8, Q9, Q10, Q11, Q12, Q13, Q14, Q15, Q16, Q17, Q18, Q19, Q20, Q21, Q22, Q23, Q24]), "radius" : 1 * mm, "tangentPropagation" : true, "allowEdgeOverflow" : false});
        }
    });
